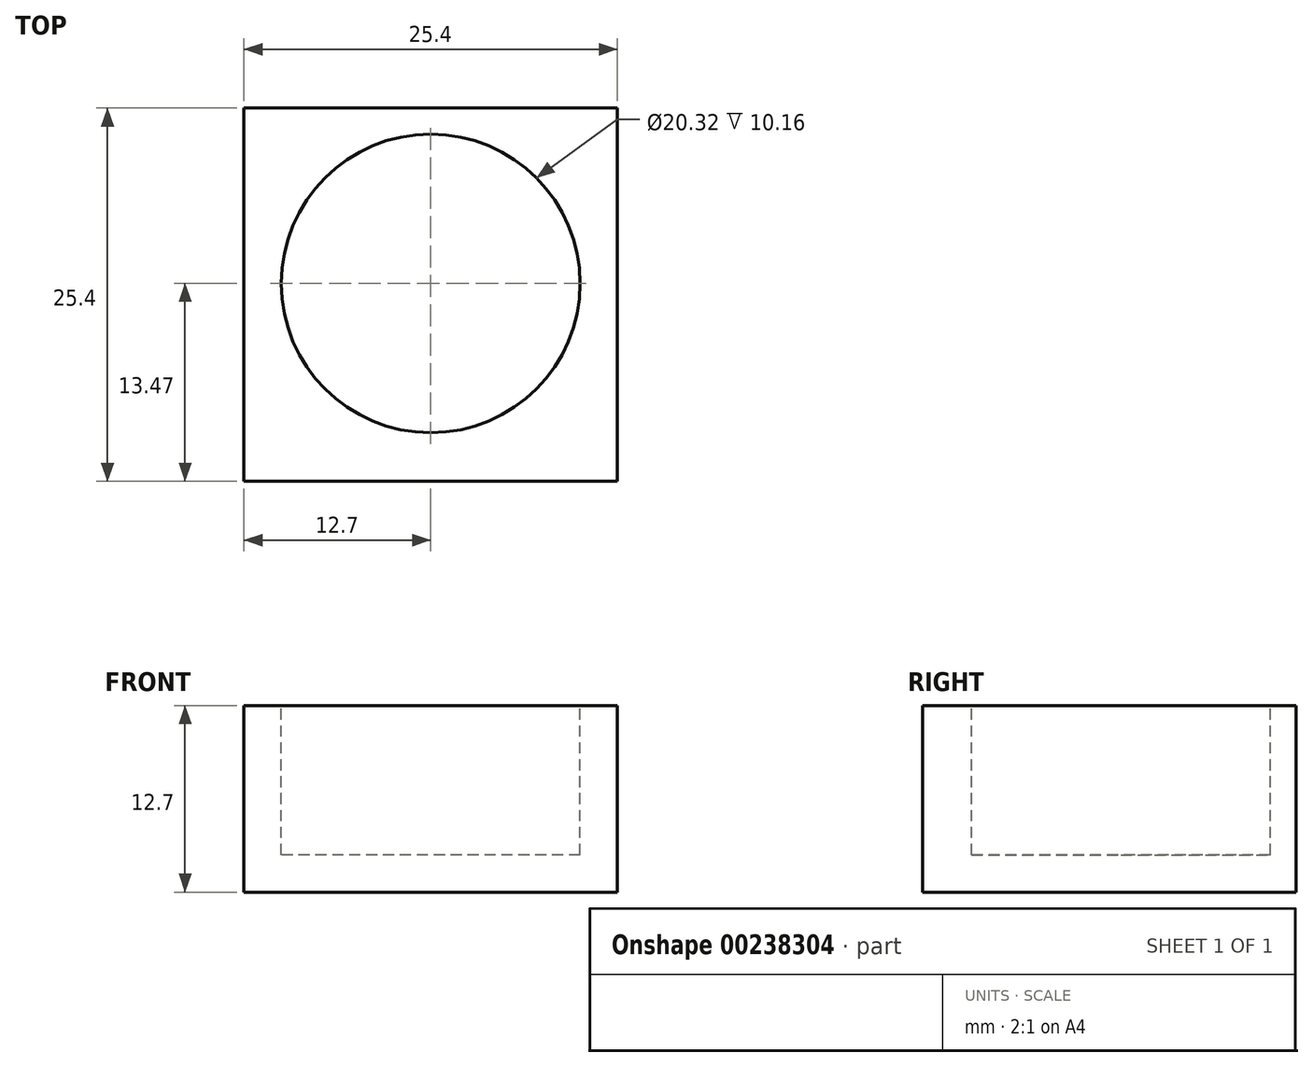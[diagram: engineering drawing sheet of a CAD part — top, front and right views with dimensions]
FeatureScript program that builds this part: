
annotation { "Feature Type Name" : "Feature", "Feature Type Description" : "" }
export const myFeature = defineFeature(function(context is Context, id is Id, definition is map)
    precondition{}
    {
        {
            var Q0;
            Q0=qCreatedBy(makeId("Top.planeOp"),FACE);
            var sketch = newSketch(context, id + "F0", { "sketchPlane" : qUnion([Q0])});
            skLineSegment(sketch, "E0.bottom", {"start": v(0, 11.93) * mm, "end": v(25.4, 11.93) * mm});
            skLineSegment(sketch, "E0.top", {"start": v(0, -13.47) * mm, "end": v(25.4, -13.47) * mm});
            skLineSegment(sketch, "E0.left", {"start": v(0, 11.93) * mm, "end": v(0, -13.47) * mm});
            skLineSegment(sketch, "E0.right", {"start": v(25.4, 11.93) * mm, "end": v(25.4, -13.47) * mm});
            skSolve(sketch);
        }
        {
            var Q0;
            Q0=makeQuery(id+"F0.imprint","IMPRINT",FACE,{"disambiguationData":[TD([[makeQuery(id+"F0.imprint","IMPRINT",EDGE,{"derivedFrom":sQuery(id+"F0.wireOp",EDGE,"E0.bottom")}),-1.0]])]});
            extrude(context, id + "F1", {"entities" : qUnion([Q0]), "depth" : 12.7 * mm});
        }
        {
            var Q0;
            Q0=makeQuery(id+"F1.opExtrude","CAP_FACE",FACE,{"disambiguationData":[OSD([sQuery(id+"F0.wireOp",EDGE,"E0.bottom"),sQuery(id+"F0.wireOp",EDGE,"E0.top"),sQuery(id+"F0.wireOp",EDGE,"E0.left"),sQuery(id+"F0.wireOp",EDGE,"E0.right")])],"isStart":false});
            var sketch = newSketch(context, id + "F2", { "sketchPlane" : qUnion([Q0])});
            skCircle(sketch, "E1", {"center": v(12.7, 0) * mm, "radius": 10.16 * mm});
            skPoint(sketch, "E1.centerSnap0", {"position": v(12.7, 11.93) * mm});
            skSolve(sketch);
        }
        {
            var Q0;
            Q0=makeQuery(id+"F2.imprint","IMPRINT",FACE,{"disambiguationData":[TD([[makeQuery(id+"F2.imprint","IMPRINT",EDGE,{"derivedFrom":sQuery(id+"F2.wireOp",EDGE,"E1")}),1.0]])]});
            var Q1;
            Q1=sQuery(id+"F2.wireOp",EDGE,"E1");
            extrude(context, id + "F3", {"entities" : qUnion([Q0]), "operationType" : NewBodyOperationType.REMOVE, "surfaceEntities" : qUnion([Q1]), "oppositeDirection" : true, "depth" : 10.16 * mm});
        }
    });
